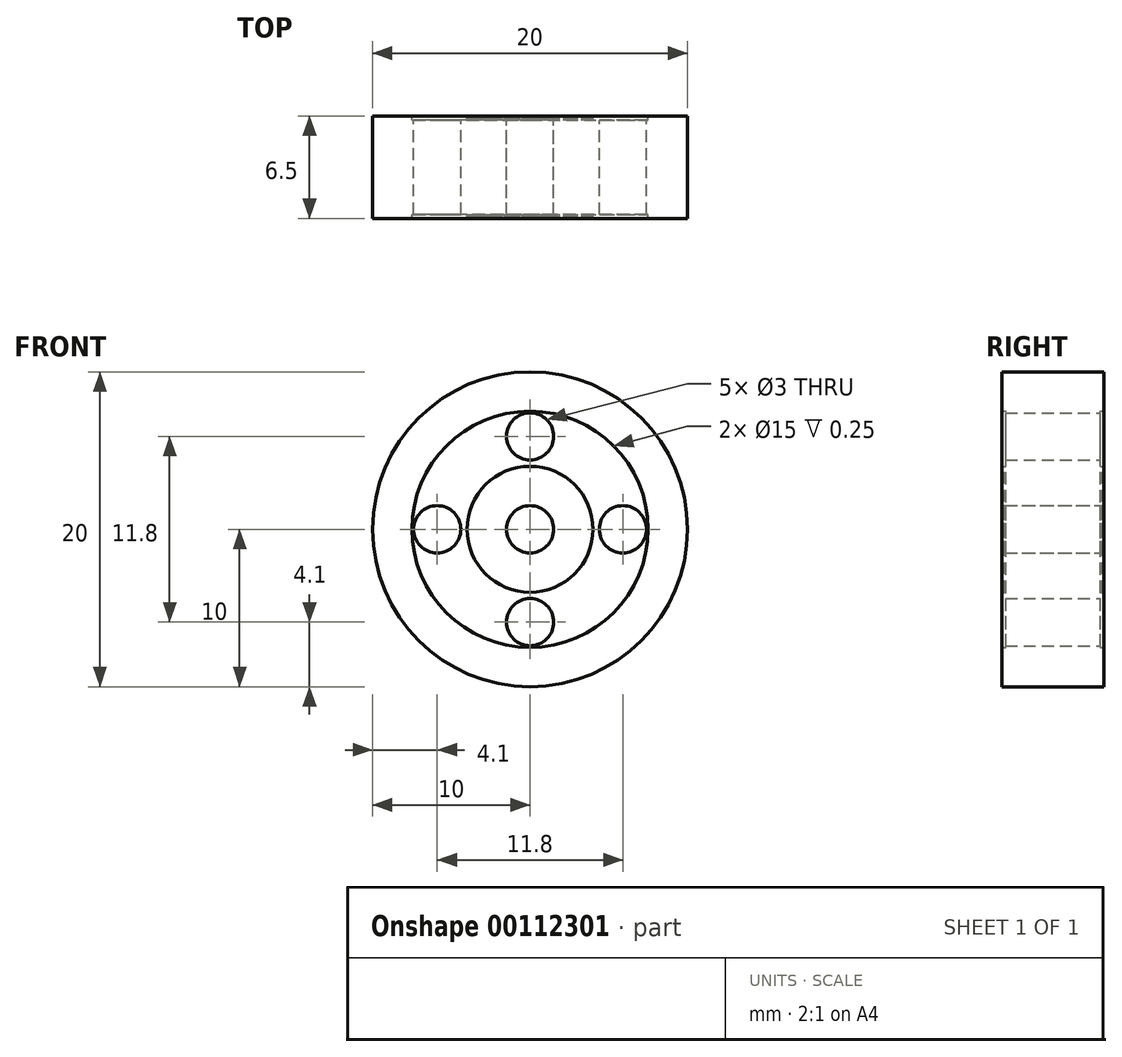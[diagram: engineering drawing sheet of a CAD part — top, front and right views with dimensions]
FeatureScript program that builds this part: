
annotation { "Feature Type Name" : "Feature", "Feature Type Description" : "" }
export const myFeature = defineFeature(function(context is Context, id is Id, definition is map)
    precondition{}
    {
        {
            var Q0;
            Q0=qCreatedBy(makeId("Front.planeOp"),FACE);
            var sketch = newSketch(context, id + "F0", { "sketchPlane" : qUnion([Q0])});
            skCircle(sketch, "E0", {"center": v(0, 0) * mm, "radius": 10 * mm});
            skCircle(sketch, "E1", {"center": v(0, 0) * mm, "radius": 4 * mm});
            skCircle(sketch, "E2", {"center": v(0, 0) * mm, "radius": 1.5 * mm});
            skCircle(sketch, "E3", {"center": v(0, 5.9) * mm, "radius": 1.5 * mm});
            skCircle(sketch, "E4.1.0", {"center": v(-5.9, 0) * mm, "radius": 1.5 * mm});
            skCircle(sketch, "E4.2.0", {"center": v(0, -5.9) * mm, "radius": 1.5 * mm});
            skCircle(sketch, "E4.3.0", {"center": v(5.9, 0) * mm, "radius": 1.5 * mm});
            skCircle(sketch, "E5", {"center": v(0, 0) * mm, "radius": 7.5 * mm});
            skSolve(sketch);
        }
        {
            var Q0;
            Q0=qSketchRegion(id+"F0",true);
            extrude(context, id + "F1", {"entities" : qUnion([Q0]), "endBound" : BoundingType.SYMMETRIC, "depth" : 6.5 * mm});
        }
        {
            var Q0;
            Q0=makeQuery(id+"F0.imprint","IMPRINT",FACE,{"disambiguationData":[TD([[makeQuery(id+"F0.imprint","IMPRINT",EDGE,{"derivedFrom":sQuery(id+"F0.wireOp",EDGE,"E1")}),-1.0]])]});
            extrude(context, id + "F2", {"entities" : qUnion([Q0]), "operationType" : NewBodyOperationType.ADD, "endBound" : BoundingType.SYMMETRIC, "depth" : 6 * mm});
        }
        {
            var Q0;
            Q0=makeQuery(id+"F0.imprint","IMPRINT",FACE,{"disambiguationData":[TD([[makeQuery(id+"F0.imprint","IMPRINT",EDGE,{"derivedFrom":sQuery(id+"F0.wireOp",EDGE,"E1")}),1.0]])]});
            extrude(context, id + "F3", {"entities" : qUnion([Q0]), "operationType" : NewBodyOperationType.ADD, "endBound" : BoundingType.SYMMETRIC, "depth" : 6.25 * mm});
        }
    });
